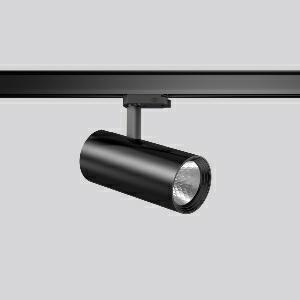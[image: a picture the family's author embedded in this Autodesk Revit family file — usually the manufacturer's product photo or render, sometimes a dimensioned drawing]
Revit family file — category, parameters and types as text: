
# Revit family: deecos_s_mini_742203_003_3_76_ff16
name_source: partatom
category: Lighting Fixtures
units: mm (PartAtom-declared; Revit-internal decimal feet)

## family parameters
Cut with Voids When Loaded = No
Host = Face
Light Source = No
Part Type = Normal
Room Calculation Point = No
Round Connector Dimension = Use Diameter
Shared = No

## types (1)
- DEECOS S mini (1 x LED Modul 935, 3700 lm, 3500)
    Apparent Load = 29 VA
    Approval mark = CE
    CIE Flux Codes = 100 100 100 100 100
    Color Rendering = 92
    Color Temperature = 3500
    Default Elevation = 1800 mm
    Description = Series: DEECOS S mini
LED surface-mounted projector in modern design with no visible cooling ribs. Housing: die-cast aluminium, powder-coated. Rotation range: 356°. Swivel range: 90°. Black plastic ring and recessed LED to prevent glare from the side. Optical assembly with reflector made of MIRO-Silver with 98% total light reflection for outstanding efficiency - can be changed without tools. Best colour rendering index Ra>90. With adapter for RZB 3-circuit DALI tracks. Suitable for Track on ceiling, Wall track. High quality converter without flickering and stroboscopic effect. The following accessories can be mounted without use of tools: interchangeable lenses, decorative glasses, honeycomb louvre, clear and frosted diffusers, white interchangeable plastic ring. 
Colour: deep black, matt (RAL 9005)
Diameter: 87 mm
Height: 214 mm
Lamp: LED
Socket: without socket
Colour temperature: 3500K
Colour rendering index (CRI): 92
System power: 29 W
Rated luminous flux: 3700 lm
Luminous efficiency: 128 lm/W
Control gear: Converter, dimmable, DALI
Protection class: I
Type of protection: IP 20
    Height = 214 mm
    Lamp = 1 x LED Modul 935
    Lamp Light Flux = 3700 lm
    Lamp count = 1
    Length = 87 mm
    Lifetime = 50000 h
    Luminous efficacy = 128 lm/W
    Manufacturer = RZB
    ModVariant = No
    Model = 742203.003.3.76
    Mounting Place = Ceiling
    Mounting Type = Rail mounted
    Number of Poles = 1
    OnlyDefault = Yes
    Power Factor = 1
    Product Name = DEECOS S mini
    Product group = Track mounted projectors
    ProductGroupID = 301
    Protection Class = Protection class I
    Protection Degree = IP 20
    RLX_Detail_Level = 1
    RLX_Emergency_Light_Flux = 0 lm
    RLX_Emergency_Type = 0
    RLX_Emergency_Type_DB = No
    RlxData = <blob elided: 38677 chars, md5=7aa6f0ad>
    Socket = socket
    Standby Power = 0 W
    System Light Flux = 3700 lm
    System Power = 29 W
    Type Comments = Product without accessories
    Type Image = 741926.003.jpg
    URL = http://relux.com
    VarID = ---
    Voltage = 230 V
    Voltage Range = 220-240 V
    Weight = 0.00 kg
    Width = 0 mm  [stored 0 ft]

note: [stored X ft] marks values corroborated as IEEE doubles in the binary element streams (Revit-internal decimal feet)

## geometry (parser evidence)
native form markers: Blend x4, Sweep x13
no freeform markers — native parametric forms only
